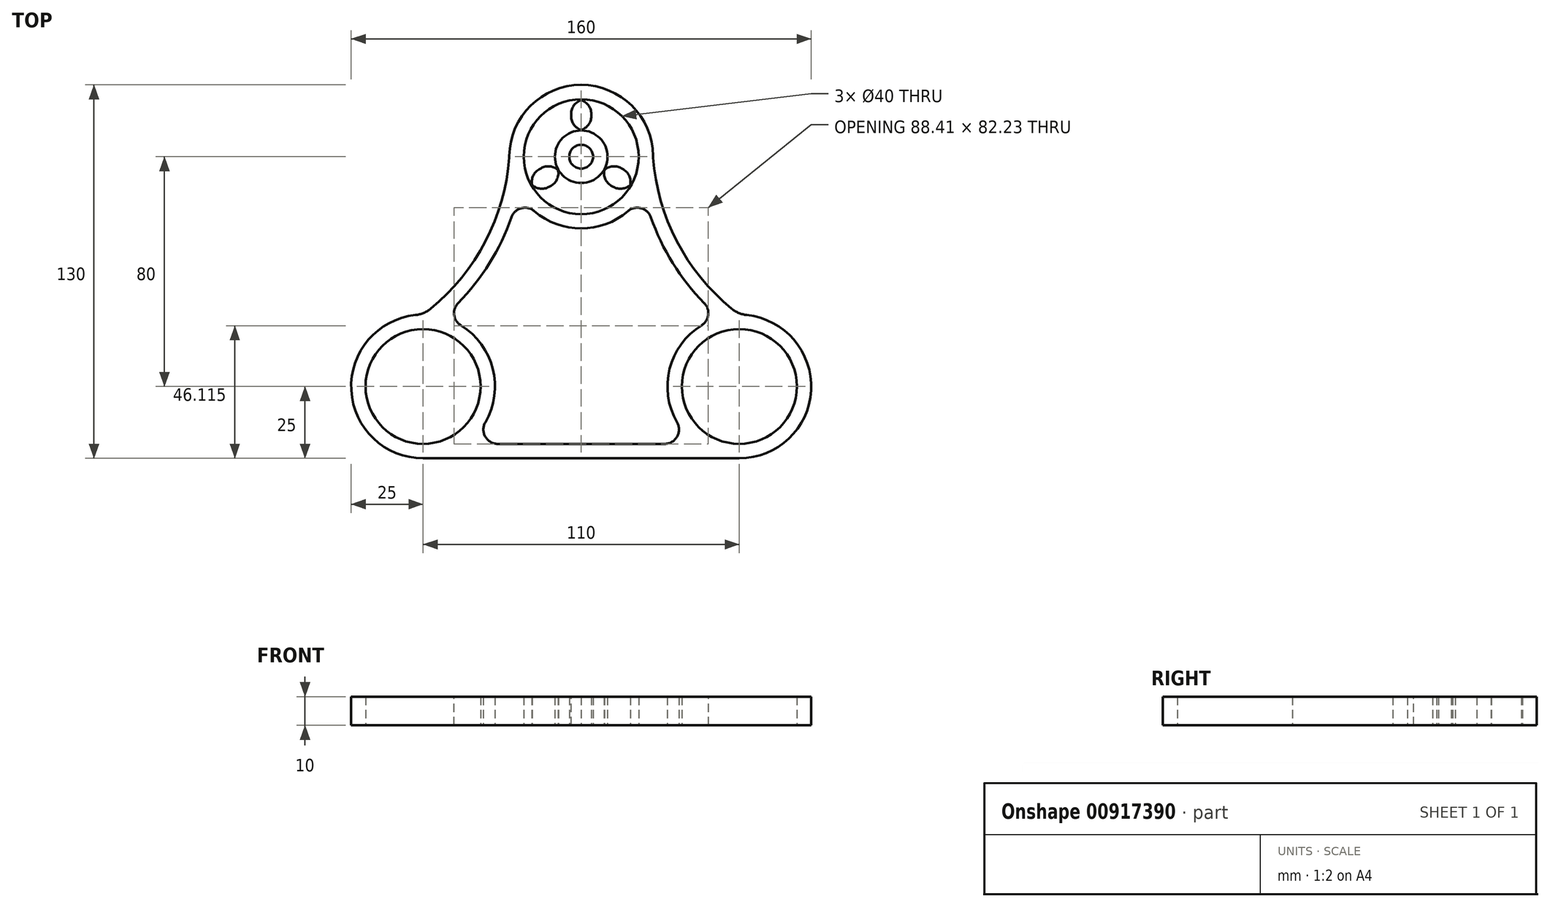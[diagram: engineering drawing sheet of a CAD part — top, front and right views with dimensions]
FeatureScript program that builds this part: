
annotation { "Feature Type Name" : "Feature", "Feature Type Description" : "" }
export const myFeature = defineFeature(function(context is Context, id is Id, definition is map)
    precondition{}
    {
        {
            assignVariable(context, id + "F0", {"name" : "height", "anyValue" : 10});
        }
        {
            var Q0;
            Q0=qCreatedBy(makeId("Top.planeOp"),FACE);
            var sketch = newSketch(context, id + "F1", { "sketchPlane" : qUnion([Q0])});
            skCircle(sketch, "E0", {"center": v(0, 0) * mm, "radius": 100 * mm, "construction": true});
            skCircle(sketch, "E1", {"center": v(0, 0) * mm, "radius": 25 * mm});
            skLineSegment(sketch, "E2", {"start": v(-55, -80) * mm, "end": v(55, -80) * mm, "construction": true});
            skPoint(sketch, "E3", {"position": v(0, -80) * mm});
            skCircle(sketch, "E4", {"center": v(-55, -80) * mm, "radius": 25 * mm});
            skCircle(sketch, "E5.MirrorC", {"center": v(55, -80) * mm, "radius": 25 * mm});
            skLineSegment(sketch, "E6", {"start": v(-55, -105) * mm, "end": v(55, -105) * mm});
            skLineSegment(sketch, "E7", {"start": v(0, 0) * mm, "end": v(-50.14, 50.14) * mm, "construction": true});
            skArc(sketch, "E8", {"start": v(-55, -55) * mm, "mid": v(-33.98, -30.78) * mm, "end": v(-25, 0) * mm});
            skArc(sketch, "E9.MirrorCS", {"start": v(55, -55) * mm, "mid": v(33.98, -30.78) * mm, "end": v(25, 0) * mm});
            skCircle(sketch, "E10", {"center": v(0, 0) * mm, "radius": 4.15 * mm});
            skCircle(sketch, "E11", {"center": v(0, 0) * mm, "radius": 20 * mm});
            skCircle(sketch, "E12", {"center": v(-55, -80) * mm, "radius": 20 * mm});
            skCircle(sketch, "E13.MirrorC", {"center": v(55, -80) * mm, "radius": 20 * mm});
            skCircle(sketch, "E14", {"center": v(0, 0) * mm, "radius": 9.15 * mm});
            skLineSegment(sketch, "E15", {"start": v(-3.5, 8.45) * mm, "end": v(-3.5, 19.7) * mm});
            skLineSegment(sketch, "E16.MirrorCS", {"start": v(3.5, 8.45) * mm, "end": v(3.5, 19.7) * mm});
            skSolve(sketch);
        }
        {
            var Q0;
            Q0 = qSketchRegion(id + "F1", true);
            extrude(context, id + "F2", {"entities" : qUnion([Q0]), "depth" : (getVariable(context, 'height')) * mm, "offsetDistance" : 25 * mm});
        }
        {
            var Q0;
            Q0=makeQuery(id+"F2.opExtrude","CAP_FACE",FACE,{"disambiguationData":[OSD([sQuery(id+"F1.wireOp",EDGE,"E1"),sQuery(id+"F1.wireOp",EDGE,"E4"),sQuery(id+"F1.wireOp",EDGE,"E5.MirrorC"),sQuery(id+"F1.wireOp",EDGE,"E6"),sQuery(id+"F1.wireOp",EDGE,"E8"),sQuery(id+"F1.wireOp",EDGE,"E9.MirrorCS"),sQuery(id+"F1.wireOp",EDGE,"E11"),sQuery(id+"F1.wireOp",EDGE,"E12"),sQuery(id+"F1.wireOp",EDGE,"E13.MirrorC")])],"isStart":false});
            shell(context, id + "F3", {"entities" : qUnion([Q0]), "thickness" : 5 * mm});
        }
        {
            var Q0;
            Q0=makeQuery(id+"F3.opShell","OFFSET_FACE",FACE,{"disambiguationData":[OSD([sQuery(id+"F1.wireOp",EDGE,"E1"),sQuery(id+"F1.wireOp",EDGE,"E4"),sQuery(id+"F1.wireOp",EDGE,"E5.MirrorC"),sQuery(id+"F1.wireOp",EDGE,"E6"),sQuery(id+"F1.wireOp",EDGE,"E8"),sQuery(id+"F1.wireOp",EDGE,"E9.MirrorCS"),sQuery(id+"F1.wireOp",EDGE,"E11"),sQuery(id+"F1.wireOp",EDGE,"E12"),sQuery(id+"F1.wireOp",EDGE,"E13.MirrorC")])]});
            extrude(context, id + "F4", {"entities" : qUnion([Q0]), "operationType" : NewBodyOperationType.REMOVE, "endBound" : BoundingType.THROUGH_ALL, "oppositeDirection" : true, "depth" : 25 * mm, "offsetDistance" : 25 * mm});
        }
        {
            var Q0;
            Q0=makeQuery(id+"F1.imprint","IMPRINT",FACE,{"disambiguationData":[TD([[makeQuery(id+"F1.imprint","IMPRINT",EDGE,{"derivedFrom":sQuery(id+"F1.wireOp",EDGE,"E10")}),-1.0]])]});
            var Q1;
            Q1=makeQuery(id+"F2.opExtrude","CAP_FACE",FACE,{"disambiguationData":[OSD([sQuery(id+"F1.wireOp",EDGE,"E1"),sQuery(id+"F1.wireOp",EDGE,"E4"),sQuery(id+"F1.wireOp",EDGE,"E5.MirrorC"),sQuery(id+"F1.wireOp",EDGE,"E6"),sQuery(id+"F1.wireOp",EDGE,"E8"),sQuery(id+"F1.wireOp",EDGE,"E9.MirrorCS"),sQuery(id+"F1.wireOp",EDGE,"E11"),sQuery(id+"F1.wireOp",EDGE,"E12"),sQuery(id+"F1.wireOp",EDGE,"E13.MirrorC")])],"isStart":false});
            extrude(context, id + "F5", {"entities" : qUnion([Q0]), "endBound" : BoundingType.UP_TO_SURFACE, "depth" : 25 * mm, "endBoundEntityFace" : qUnion([Q1]), "offsetDistance" : 25 * mm});
        }
        {
            var Q0;
            {var subQ0=sQuery(id+"F1.wireOp",EDGE,"E15");Q0=makeQuery(id+"F1.imprint","IMPRINT",FACE,{"disambiguationData":[TD([[makeQuery(id+"F1.imprint","IMPRINT",EDGE,{"derivedFrom":subQ0}),-1.0]])]});}
            var Q1;
            Q1=makeQuery(id+"F2.opExtrude","CAP_FACE",FACE,{"disambiguationData":[OSD([sQuery(id+"F1.wireOp",EDGE,"E1"),sQuery(id+"F1.wireOp",EDGE,"E4"),sQuery(id+"F1.wireOp",EDGE,"E5.MirrorC"),sQuery(id+"F1.wireOp",EDGE,"E6"),sQuery(id+"F1.wireOp",EDGE,"E8"),sQuery(id+"F1.wireOp",EDGE,"E9.MirrorCS"),sQuery(id+"F1.wireOp",EDGE,"E11"),sQuery(id+"F1.wireOp",EDGE,"E12"),sQuery(id+"F1.wireOp",EDGE,"E13.MirrorC")])],"isStart":false});
            extrude(context, id + "F6", {"entities" : qUnion([Q0]), "endBound" : BoundingType.UP_TO_SURFACE, "depth" : 25 * mm, "endBoundEntityFace" : qUnion([Q1]), "offsetDistance" : 25 * mm});
        }
        {
            var Q0;
            Q0=qCreatedBy(makeId("Front.planeOp"),FACE);
            var sketch = newSketch(context, id + "F7", { "sketchPlane" : qUnion([Q0])});
            skLineSegment(sketch, "E17", {"start": v(0, 57.22) * mm, "end": v(0, -63.95) * mm, "construction": true});
            skSolve(sketch);
        }
        {
            var Q0;
            Q0=makeQuery(id+"F6.opExtrude","SWEPT_BODY",BODY,{"disambiguationData":[OSD([sQuery(id+"F1.wireOp",EDGE,"E11"),sQuery(id+"F1.wireOp",EDGE,"E14"),sQuery(id+"F1.wireOp",EDGE,"E15"),sQuery(id+"F1.wireOp",EDGE,"E16.MirrorCS")])]});
            var Q1;
            Q1=sQuery(id+"F7.wireOp",EDGE,"E17");
            circularPattern(context, id + "F8", {"entities" : qUnion([Q0]), "axis" : qUnion([Q1]), "angle" : 360 * degree, "instanceCount" : 3, "equalSpace" : true});
        }
        {
            var Q0;
            Q0=makeQuery(id+"F6.opExtrude","SWEPT_EDGE",EDGE,{"disambiguationData":[OSD([sQuery(id+"F1.wireOp",EDGE,"E14"),sQuery(id+"F1.wireOp",EDGE,"E16.MirrorCS")])]});
            var Q1;
            Q1=makeQuery(id+"F6.opExtrude","SWEPT_EDGE",EDGE,{"disambiguationData":[OSD([sQuery(id+"F1.wireOp",EDGE,"E11"),sQuery(id+"F1.wireOp",EDGE,"E16.MirrorCS")])]});
            var Q2;
            Q2=makeQuery(id+"F8.opPattern","COPY",EDGE,{"derivedFrom":makeQuery(id+"F6.opExtrude","SWEPT_EDGE",EDGE,{"disambiguationData":[OSD([sQuery(id+"F1.wireOp",EDGE,"E14"),sQuery(id+"F1.wireOp",EDGE,"E15")])]}),"instanceName":"1"});
            var Q3;
            Q3=makeQuery(id+"F8.opPattern","COPY",EDGE,{"derivedFrom":makeQuery(id+"F6.opExtrude","SWEPT_EDGE",EDGE,{"disambiguationData":[OSD([sQuery(id+"F1.wireOp",EDGE,"E11"),sQuery(id+"F1.wireOp",EDGE,"E15")])]}),"instanceName":"1"});
            var Q4;
            Q4=makeQuery(id+"F8.opPattern","COPY",EDGE,{"derivedFrom":makeQuery(id+"F6.opExtrude","SWEPT_EDGE",EDGE,{"disambiguationData":[OSD([sQuery(id+"F1.wireOp",EDGE,"E11"),sQuery(id+"F1.wireOp",EDGE,"E16.MirrorCS")])]}),"instanceName":"1"});
            var Q5;
            Q5=makeQuery(id+"F8.opPattern","COPY",EDGE,{"derivedFrom":makeQuery(id+"F6.opExtrude","SWEPT_EDGE",EDGE,{"disambiguationData":[OSD([sQuery(id+"F1.wireOp",EDGE,"E11"),sQuery(id+"F1.wireOp",EDGE,"E15")])]}),"instanceName":"2"});
            var Q6;
            Q6=makeQuery(id+"F8.opPattern","COPY",EDGE,{"derivedFrom":makeQuery(id+"F6.opExtrude","SWEPT_EDGE",EDGE,{"disambiguationData":[OSD([sQuery(id+"F1.wireOp",EDGE,"E14"),sQuery(id+"F1.wireOp",EDGE,"E15")])]}),"instanceName":"2"});
            var Q7;
            Q7=makeQuery(id+"F8.opPattern","COPY",EDGE,{"derivedFrom":makeQuery(id+"F6.opExtrude","SWEPT_EDGE",EDGE,{"disambiguationData":[OSD([sQuery(id+"F1.wireOp",EDGE,"E14"),sQuery(id+"F1.wireOp",EDGE,"E16.MirrorCS")])]}),"instanceName":"1"});
            var Q8;
            Q8=makeQuery(id+"F8.opPattern","COPY",EDGE,{"derivedFrom":makeQuery(id+"F6.opExtrude","SWEPT_EDGE",EDGE,{"disambiguationData":[OSD([sQuery(id+"F1.wireOp",EDGE,"E14"),sQuery(id+"F1.wireOp",EDGE,"E16.MirrorCS")])]}),"instanceName":"2"});
            var Q9;
            Q9=makeQuery(id+"F6.opExtrude","SWEPT_EDGE",EDGE,{"disambiguationData":[OSD([sQuery(id+"F1.wireOp",EDGE,"E14"),sQuery(id+"F1.wireOp",EDGE,"E15")])]});
            var Q10;
            Q10=makeQuery(id+"F6.opExtrude","SWEPT_EDGE",EDGE,{"disambiguationData":[OSD([sQuery(id+"F1.wireOp",EDGE,"E11"),sQuery(id+"F1.wireOp",EDGE,"E15")])]});
            var Q11;
            Q11=makeQuery(id+"F8.opPattern","COPY",EDGE,{"derivedFrom":makeQuery(id+"F6.opExtrude","SWEPT_EDGE",EDGE,{"disambiguationData":[OSD([sQuery(id+"F1.wireOp",EDGE,"E11"),sQuery(id+"F1.wireOp",EDGE,"E16.MirrorCS")])]}),"instanceName":"2"});
            fillet(context, id + "F9", {"entities" : qUnion([Q0, Q1, Q2, Q3, Q4, Q5, Q6, Q7, Q8, Q9, Q10, Q11]), "radius" : 5 * mm, "tangentPropagation" : true, "allowEdgeOverflow" : false});
        }
        {
            var Q0;
            Q0=makeQuery(id+"F2.opExtrude","SWEPT_EDGE",EDGE,{"disambiguationData":[OSD([sQuery(id+"F1.wireOp",EDGE,"E5.MirrorC"),sQuery(id+"F1.wireOp",EDGE,"E9.MirrorCS")])]});
            var Q1;
            Q1=makeQuery(id+"F2.opExtrude","SWEPT_EDGE",EDGE,{"disambiguationData":[OSD([sQuery(id+"F1.wireOp",EDGE,"E4"),sQuery(id+"F1.wireOp",EDGE,"E8")])]});
            var Q2;
            Q2=makeQuery(id+"F2.opExtrude","SWEPT_EDGE",EDGE,{"disambiguationData":[OSD([sQuery(id+"F1.wireOp",EDGE,"E1"),sQuery(id+"F1.wireOp",EDGE,"E8")])]});
            var Q3;
            Q3=makeQuery(id+"F2.opExtrude","SWEPT_EDGE",EDGE,{"disambiguationData":[OSD([sQuery(id+"F1.wireOp",EDGE,"E1"),sQuery(id+"F1.wireOp",EDGE,"E9.MirrorCS")])]});
            fillet(context, id + "F10", {"entities" : qUnion([Q0, Q1, Q2, Q3]), "radius" : 10 * mm, "tangentPropagation" : true, "allowEdgeOverflow" : false});
        }
        {
            var Q0;
            {var subQ0=sQuery(id+"F1.wireOp",EDGE,"E12");var subQ1=makeQuery(id+"F2.opExtrude","SWEPT_FACE",FACE,{"disambiguationData":[OSD([subQ0])]});var subQ2=sQuery(id+"F1.wireOp",EDGE,"E8");var subQ3=makeQuery(id+"F2.opExtrude","SWEPT_FACE",FACE,{"disambiguationData":[OSD([subQ2])]});var subQ4=sQuery(id+"F1.wireOp",EDGE,"E13.MirrorC");var subQ5=sQuery(id+"F1.wireOp",EDGE,"E11");var subQ6=sQuery(id+"F1.wireOp",EDGE,"E9.MirrorCS");var subQ7=sQuery(id+"F1.wireOp",EDGE,"E6");var subQ8=sQuery(id+"F1.wireOp",EDGE,"E5.MirrorC");var subQ9=sQuery(id+"F1.wireOp",EDGE,"E4");var subQ10=sQuery(id+"F1.wireOp",EDGE,"E1");Q0=makeQuery(id+"F4.boolean.opBoolean","MERGE",EDGE,{"derivedFrom":[makeQuery(id+"F3.opShell","TWEAK_EDGE",EDGE,{"derivedFrom":[subQ3,subQ1]})],"fromTools":[makeQuery(id+"F4.opExtrude","SWEPT_EDGE",EDGE,{"disambiguationData":[OSD([subQ10,subQ9,subQ8,subQ7,subQ2,subQ6,subQ5,subQ0,subQ4]),TDD([makeQuery(id+"F3.opShell","TWEAK_VERTEX",VERTEX,{"derivedFrom":[makeQuery(id+"F2.opExtrude","CAP_FACE",FACE,{"disambiguationData":[OSD([subQ10,subQ9,subQ8,subQ7,subQ2,subQ6,subQ5,subQ0,subQ4])],"isStart":true}),subQ3,subQ1]})])]})]});}
            var Q1;
            {var subQ0=sQuery(id+"F1.wireOp",EDGE,"E12");var subQ1=makeQuery(id+"F2.opExtrude","SWEPT_FACE",FACE,{"disambiguationData":[OSD([subQ0])]});var subQ2=sQuery(id+"F1.wireOp",EDGE,"E6");var subQ3=makeQuery(id+"F2.opExtrude","SWEPT_FACE",FACE,{"disambiguationData":[OSD([subQ2])]});var subQ4=sQuery(id+"F1.wireOp",EDGE,"E13.MirrorC");var subQ5=sQuery(id+"F1.wireOp",EDGE,"E11");var subQ6=sQuery(id+"F1.wireOp",EDGE,"E9.MirrorCS");var subQ7=sQuery(id+"F1.wireOp",EDGE,"E8");var subQ8=sQuery(id+"F1.wireOp",EDGE,"E5.MirrorC");var subQ9=sQuery(id+"F1.wireOp",EDGE,"E4");var subQ10=sQuery(id+"F1.wireOp",EDGE,"E1");Q1=makeQuery(id+"F4.boolean.opBoolean","MERGE",EDGE,{"derivedFrom":[makeQuery(id+"F3.opShell","TWEAK_EDGE",EDGE,{"derivedFrom":[subQ3,subQ1]})],"fromTools":[makeQuery(id+"F4.opExtrude","SWEPT_EDGE",EDGE,{"disambiguationData":[OSD([subQ10,subQ9,subQ8,subQ2,subQ7,subQ6,subQ5,subQ0,subQ4]),TDD([makeQuery(id+"F3.opShell","TWEAK_VERTEX",VERTEX,{"derivedFrom":[makeQuery(id+"F2.opExtrude","CAP_FACE",FACE,{"disambiguationData":[OSD([subQ10,subQ9,subQ8,subQ2,subQ7,subQ6,subQ5,subQ0,subQ4])],"isStart":true}),subQ3,subQ1]})])]})]});}
            var Q2;
            {var subQ0=sQuery(id+"F1.wireOp",EDGE,"E13.MirrorC");var subQ1=makeQuery(id+"F2.opExtrude","SWEPT_FACE",FACE,{"disambiguationData":[OSD([subQ0])]});var subQ2=sQuery(id+"F1.wireOp",EDGE,"E6");var subQ3=makeQuery(id+"F2.opExtrude","SWEPT_FACE",FACE,{"disambiguationData":[OSD([subQ2])]});var subQ4=sQuery(id+"F1.wireOp",EDGE,"E12");var subQ5=sQuery(id+"F1.wireOp",EDGE,"E11");var subQ6=sQuery(id+"F1.wireOp",EDGE,"E9.MirrorCS");var subQ7=sQuery(id+"F1.wireOp",EDGE,"E8");var subQ8=sQuery(id+"F1.wireOp",EDGE,"E5.MirrorC");var subQ9=sQuery(id+"F1.wireOp",EDGE,"E4");var subQ10=sQuery(id+"F1.wireOp",EDGE,"E1");Q2=makeQuery(id+"F4.boolean.opBoolean","MERGE",EDGE,{"derivedFrom":[makeQuery(id+"F3.opShell","TWEAK_EDGE",EDGE,{"derivedFrom":[subQ3,subQ1]})],"fromTools":[makeQuery(id+"F4.opExtrude","SWEPT_EDGE",EDGE,{"disambiguationData":[OSD([subQ10,subQ9,subQ8,subQ2,subQ7,subQ6,subQ5,subQ4,subQ0]),TDD([makeQuery(id+"F3.opShell","TWEAK_VERTEX",VERTEX,{"derivedFrom":[makeQuery(id+"F2.opExtrude","CAP_FACE",FACE,{"disambiguationData":[OSD([subQ10,subQ9,subQ8,subQ2,subQ7,subQ6,subQ5,subQ4,subQ0])],"isStart":true}),subQ3,subQ1]})])]})]});}
            var Q3;
            {var subQ0=sQuery(id+"F1.wireOp",EDGE,"E13.MirrorC");var subQ1=makeQuery(id+"F2.opExtrude","SWEPT_FACE",FACE,{"disambiguationData":[OSD([subQ0])]});var subQ2=sQuery(id+"F1.wireOp",EDGE,"E9.MirrorCS");var subQ3=makeQuery(id+"F2.opExtrude","SWEPT_FACE",FACE,{"disambiguationData":[OSD([subQ2])]});var subQ4=sQuery(id+"F1.wireOp",EDGE,"E12");var subQ5=sQuery(id+"F1.wireOp",EDGE,"E11");var subQ6=sQuery(id+"F1.wireOp",EDGE,"E8");var subQ7=sQuery(id+"F1.wireOp",EDGE,"E6");var subQ8=sQuery(id+"F1.wireOp",EDGE,"E5.MirrorC");var subQ9=sQuery(id+"F1.wireOp",EDGE,"E4");var subQ10=sQuery(id+"F1.wireOp",EDGE,"E1");Q3=makeQuery(id+"F4.boolean.opBoolean","MERGE",EDGE,{"derivedFrom":[makeQuery(id+"F3.opShell","TWEAK_EDGE",EDGE,{"derivedFrom":[subQ3,subQ1]})],"fromTools":[makeQuery(id+"F4.opExtrude","SWEPT_EDGE",EDGE,{"disambiguationData":[OSD([subQ10,subQ9,subQ8,subQ7,subQ6,subQ2,subQ5,subQ4,subQ0]),TDD([makeQuery(id+"F3.opShell","TWEAK_VERTEX",VERTEX,{"derivedFrom":[makeQuery(id+"F2.opExtrude","CAP_FACE",FACE,{"disambiguationData":[OSD([subQ10,subQ9,subQ8,subQ7,subQ6,subQ2,subQ5,subQ4,subQ0])],"isStart":true}),subQ3,subQ1]})])]})]});}
            var Q4;
            {var subQ0=sQuery(id+"F1.wireOp",EDGE,"E11");var subQ1=makeQuery(id+"F2.opExtrude","SWEPT_FACE",FACE,{"disambiguationData":[OSD([subQ0])]});var subQ2=sQuery(id+"F1.wireOp",EDGE,"E9.MirrorCS");var subQ3=makeQuery(id+"F2.opExtrude","SWEPT_FACE",FACE,{"disambiguationData":[OSD([subQ2])]});var subQ4=sQuery(id+"F1.wireOp",EDGE,"E13.MirrorC");var subQ5=sQuery(id+"F1.wireOp",EDGE,"E12");var subQ6=sQuery(id+"F1.wireOp",EDGE,"E8");var subQ7=sQuery(id+"F1.wireOp",EDGE,"E6");var subQ8=sQuery(id+"F1.wireOp",EDGE,"E5.MirrorC");var subQ9=sQuery(id+"F1.wireOp",EDGE,"E4");var subQ10=sQuery(id+"F1.wireOp",EDGE,"E1");Q4=makeQuery(id+"F4.boolean.opBoolean","MERGE",EDGE,{"derivedFrom":[makeQuery(id+"F3.opShell","TWEAK_EDGE",EDGE,{"derivedFrom":[subQ3,subQ1]})],"fromTools":[makeQuery(id+"F4.opExtrude","SWEPT_EDGE",EDGE,{"disambiguationData":[OSD([subQ10,subQ9,subQ8,subQ7,subQ6,subQ2,subQ0,subQ5,subQ4]),TDD([makeQuery(id+"F3.opShell","TWEAK_VERTEX",VERTEX,{"derivedFrom":[makeQuery(id+"F2.opExtrude","CAP_FACE",FACE,{"disambiguationData":[OSD([subQ10,subQ9,subQ8,subQ7,subQ6,subQ2,subQ0,subQ5,subQ4])],"isStart":true}),subQ3,subQ1]})])]})]});}
            var Q5;
            {var subQ0=sQuery(id+"F1.wireOp",EDGE,"E11");var subQ1=makeQuery(id+"F2.opExtrude","SWEPT_FACE",FACE,{"disambiguationData":[OSD([subQ0])]});var subQ2=sQuery(id+"F1.wireOp",EDGE,"E8");var subQ3=makeQuery(id+"F2.opExtrude","SWEPT_FACE",FACE,{"disambiguationData":[OSD([subQ2])]});var subQ4=sQuery(id+"F1.wireOp",EDGE,"E13.MirrorC");var subQ5=sQuery(id+"F1.wireOp",EDGE,"E12");var subQ6=sQuery(id+"F1.wireOp",EDGE,"E9.MirrorCS");var subQ7=sQuery(id+"F1.wireOp",EDGE,"E6");var subQ8=sQuery(id+"F1.wireOp",EDGE,"E5.MirrorC");var subQ9=sQuery(id+"F1.wireOp",EDGE,"E4");var subQ10=sQuery(id+"F1.wireOp",EDGE,"E1");Q5=makeQuery(id+"F4.boolean.opBoolean","MERGE",EDGE,{"derivedFrom":[makeQuery(id+"F3.opShell","TWEAK_EDGE",EDGE,{"derivedFrom":[subQ3,subQ1]})],"fromTools":[makeQuery(id+"F4.opExtrude","SWEPT_EDGE",EDGE,{"disambiguationData":[OSD([subQ10,subQ9,subQ8,subQ7,subQ2,subQ6,subQ0,subQ5,subQ4]),TDD([makeQuery(id+"F3.opShell","TWEAK_VERTEX",VERTEX,{"derivedFrom":[makeQuery(id+"F2.opExtrude","CAP_FACE",FACE,{"disambiguationData":[OSD([subQ10,subQ9,subQ8,subQ7,subQ2,subQ6,subQ0,subQ5,subQ4])],"isStart":true}),subQ3,subQ1]})])]})]});}
            fillet(context, id + "F11", {"entities" : qUnion([Q0, Q1, Q2, Q3, Q4, Q5]), "radius" : 5 * mm, "tangentPropagation" : true, "allowEdgeOverflow" : false});
        }
    });
